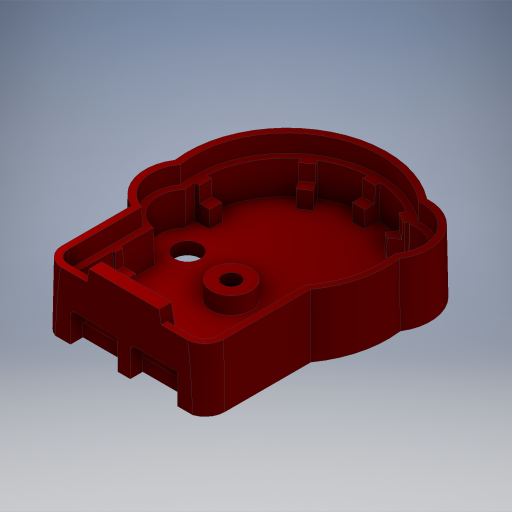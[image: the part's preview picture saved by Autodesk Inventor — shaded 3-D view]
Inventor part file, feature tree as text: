
AUTODESK INVENTOR PART (.ipt)
format: ipt  version: 2024.2 (Build 282272000, 272)  size: 420,352 bytes
history: native  units: in
note: dims shown in document units (in); Inventor stores cm internally (conversion verified against a paired STEP export)
features: fillet x1
ambient origin geometry x8: Origin, YZ Plane, XZ Plane, XY Plane, X Axis, Y Axis, Z Axis, Center Point
bodies: Solid1 (feature_tree)
feature tree (1):
  fillet  "Fillet3"  [1 undecoded]
note: 1 required parameter value undecoded (feature->parameter linkage not recoverable at this tier; creation-order binding heuristic only, values carry confidence <= 0.55)
